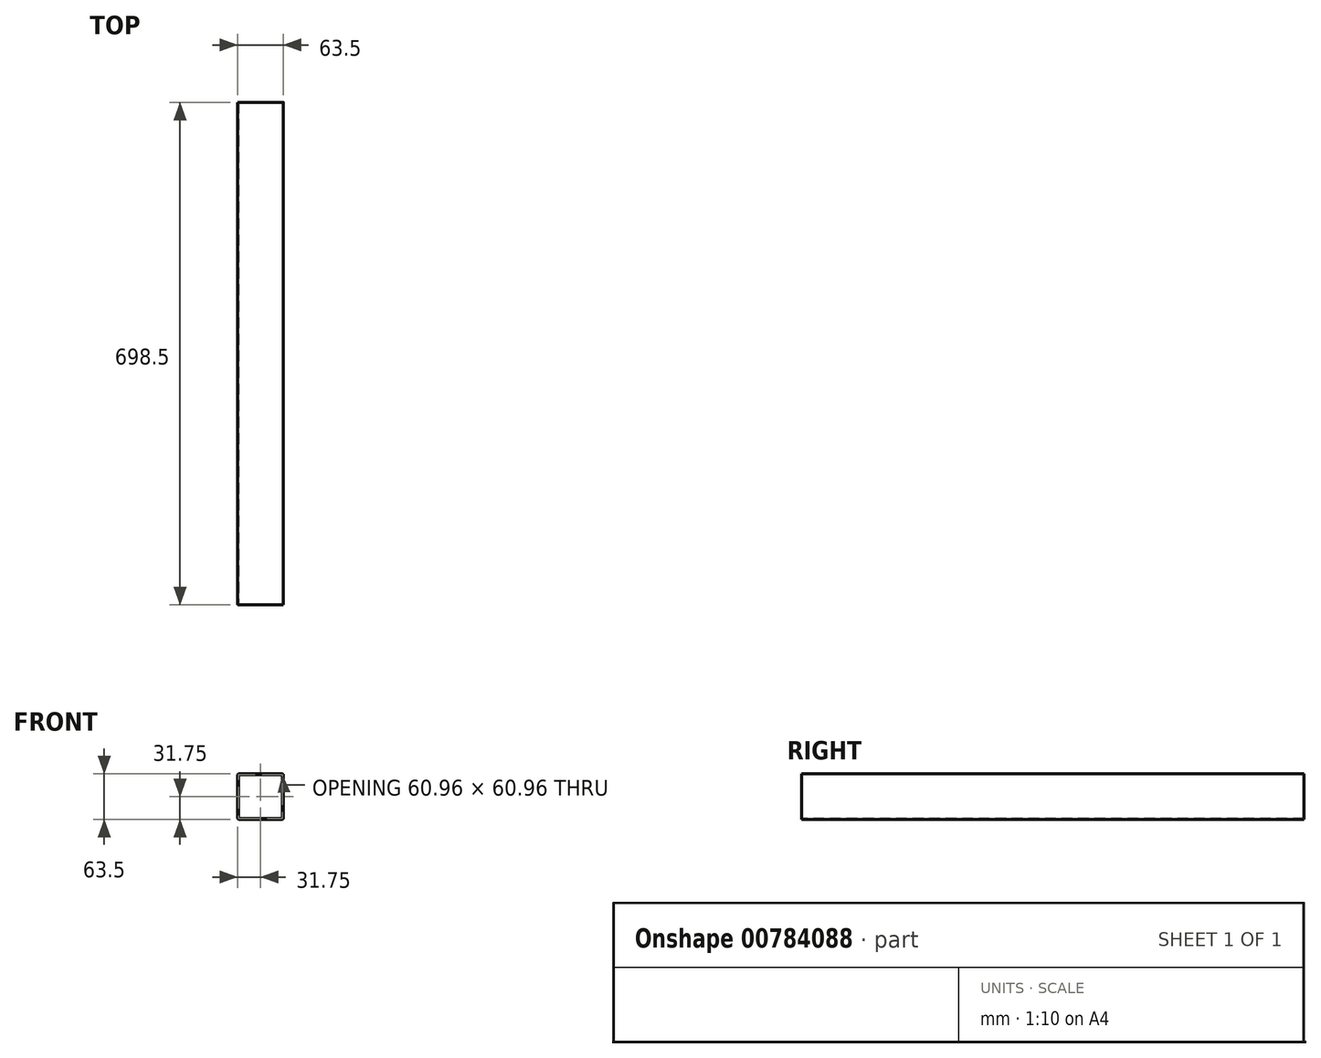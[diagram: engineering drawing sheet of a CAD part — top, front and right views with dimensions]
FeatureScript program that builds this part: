
annotation { "Feature Type Name" : "Feature", "Feature Type Description" : "" }
export const myFeature = defineFeature(function(context is Context, id is Id, definition is map)
    precondition{}
    {
        {
            var Q0;
            Q0=qCreatedBy(makeId("Front.planeOp"),FACE);
            var sketch = newSketch(context, id + "F0", { "sketchPlane" : qUnion([Q0])});
            skLineSegment(sketch, "E0.bottom", {"start": v(29.72, -31.75) * mm, "end": v(-29.72, -31.75) * mm});
            skLineSegment(sketch, "E0.top", {"start": v(29.72, 31.75) * mm, "end": v(-29.72, 31.75) * mm});
            skLineSegment(sketch, "E0.left", {"start": v(31.75, -29.72) * mm, "end": v(31.75, 29.72) * mm});
            skLineSegment(sketch, "E0.right", {"start": v(-31.75, -29.72) * mm, "end": v(-31.75, 29.72) * mm});
            skPoint(sketch, "E0.middle", {"position": v(0, 0) * mm});
            skPoint(sketch, "E1.visualSharp", {"position": v(-31.75, 31.75) * mm});
            skArc(sketch, "E1.filletArc", {"start": v(-29.72, 31.75) * mm, "mid": v(-31.15, 31.15) * mm, "end": v(-31.75, 29.72) * mm});
            skPoint(sketch, "E2.visualSharp", {"position": v(31.75, 31.75) * mm});
            skArc(sketch, "E2.filletArc", {"start": v(31.75, 29.72) * mm, "mid": v(31.15, 31.15) * mm, "end": v(29.72, 31.75) * mm});
            skPoint(sketch, "E3.visualSharp", {"position": v(31.75, -31.75) * mm});
            skArc(sketch, "E3.filletArc", {"start": v(29.72, -31.75) * mm, "mid": v(31.15, -31.15) * mm, "end": v(31.75, -29.72) * mm});
            skPoint(sketch, "E4.visualSharp", {"position": v(-31.75, -31.75) * mm});
            skArc(sketch, "E4.filletArc", {"start": v(-31.75, -29.72) * mm, "mid": v(-31.15, -31.15) * mm, "end": v(-29.72, -31.75) * mm});
            skSolve(sketch);
        }
        {
            var Q0;
            Q0 = qSketchRegion(id + "F0", true);
            extrude(context, id + "F1", {"entities" : qUnion([Q0]), "depth" : 698.5 * mm, "offsetDistance" : 25.4 * mm});
        }
        {
            var Q0;
            Q0=makeQuery(id+"F1.opExtrude","CAP_FACE",FACE,{"disambiguationData":[OSD([sQuery(id+"F0.wireOp",EDGE,"E0.bottom"),sQuery(id+"F0.wireOp",EDGE,"E0.top"),sQuery(id+"F0.wireOp",EDGE,"E0.left"),sQuery(id+"F0.wireOp",EDGE,"E0.right"),sQuery(id+"F0.wireOp",EDGE,"E1.filletArc"),sQuery(id+"F0.wireOp",EDGE,"E2.filletArc"),sQuery(id+"F0.wireOp",EDGE,"E3.filletArc"),sQuery(id+"F0.wireOp",EDGE,"E4.filletArc")])],"isStart":false});
            var sketch = newSketch(context, id + "F2", { "sketchPlane" : qUnion([Q0])});
            skLineSegment(sketch, "E5.0", {"start": v(30.48, -29.72) * mm, "end": v(30.48, 29.72) * mm});
            skArc(sketch, "E5.1", {"start": v(29.72, -30.48) * mm, "mid": v(30.26, -30.26) * mm, "end": v(30.48, -29.72) * mm});
            skArc(sketch, "E5.2", {"start": v(30.48, 29.72) * mm, "mid": v(30.26, 30.26) * mm, "end": v(29.72, 30.48) * mm});
            skLineSegment(sketch, "E5.3", {"start": v(-29.72, -30.48) * mm, "end": v(29.72, -30.48) * mm});
            skLineSegment(sketch, "E5.4", {"start": v(29.72, 30.48) * mm, "end": v(-29.72, 30.48) * mm});
            skArc(sketch, "E5.5", {"start": v(-29.72, 30.48) * mm, "mid": v(-30.26, 30.26) * mm, "end": v(-30.48, 29.72) * mm});
            skLineSegment(sketch, "E5.6", {"start": v(-30.48, 29.72) * mm, "end": v(-30.48, -29.72) * mm});
            skArc(sketch, "E5.7", {"start": v(-30.48, -29.72) * mm, "mid": v(-30.26, -30.26) * mm, "end": v(-29.72, -30.48) * mm});
            skSolve(sketch);
        }
        {
            var Q0;
            Q0 = qSketchRegion(id + "F2", true);
            extrude(context, id + "F3", {"entities" : qUnion([Q0]), "operationType" : NewBodyOperationType.REMOVE, "endBound" : BoundingType.THROUGH_ALL, "oppositeDirection" : true, "depth" : 25.4 * mm, "offsetDistance" : 25.4 * mm});
        }
    });
